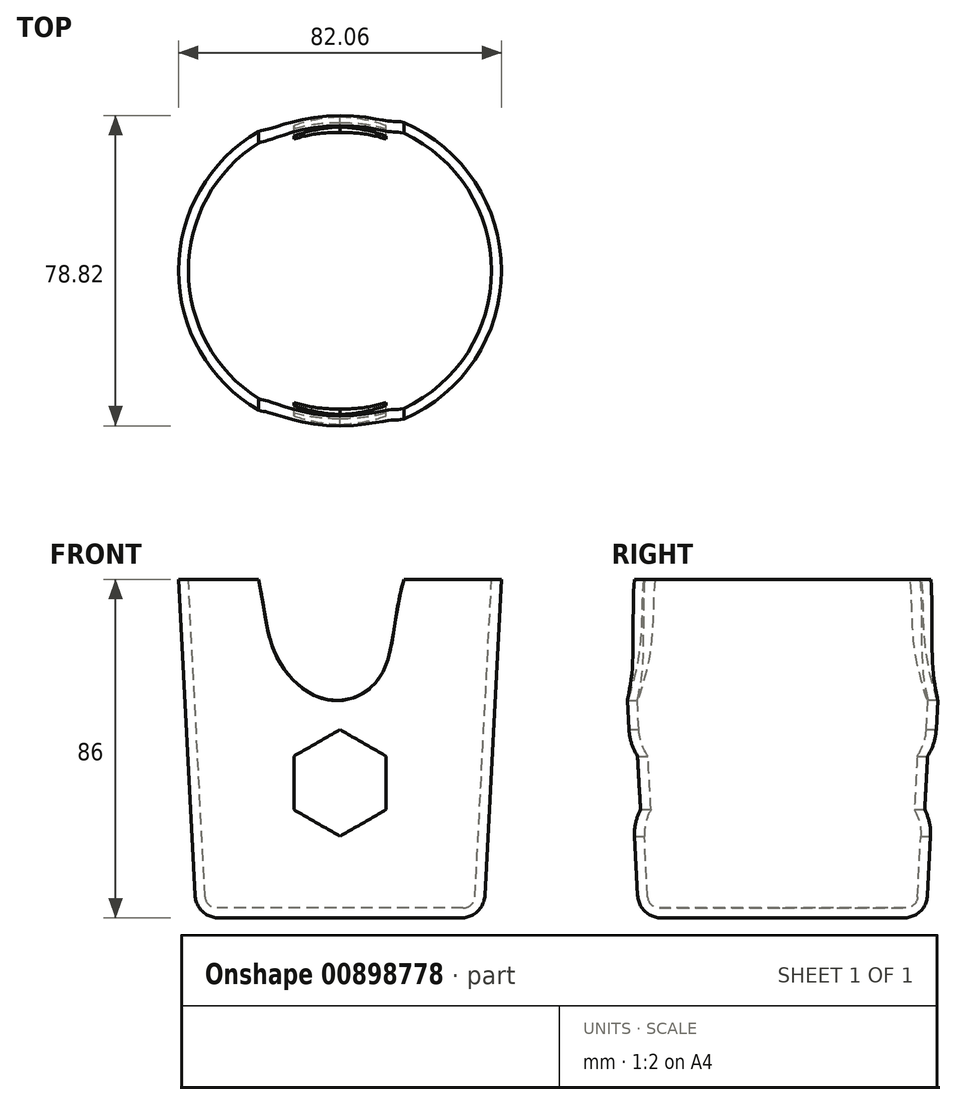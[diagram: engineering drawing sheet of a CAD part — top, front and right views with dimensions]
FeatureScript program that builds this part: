
annotation { "Feature Type Name" : "Feature", "Feature Type Description" : "" }
export const myFeature = defineFeature(function(context is Context, id is Id, definition is map)
    precondition{}
    {
        {
            var Q0;
            Q0=qCreatedBy(makeId("Top.planeOp"),FACE);
            var sketch = newSketch(context, id + "F0", { "sketchPlane" : qUnion([Q0])});
            skCircle(sketch, "E0", {"center": v(0, 0) * mm, "radius": 36.52 * mm});
            skSolve(sketch);
        }
        {
            var Q0;
            Q0=makeQuery(id+"F0.imprint","IMPRINT",FACE,{"disambiguationData":[TD([[makeQuery(id+"F0.imprint","IMPRINT",EDGE,{"derivedFrom":sQuery(id+"F0.wireOp",EDGE,"E0")}),1.0]])]});
            extrude(context, id + "F1", {"entities" : qUnion([Q0]), "depth" : 86 * mm, "offsetDistance" : 25 * mm, "hasDraft" : true, "draftAngle" : 3 * degree});
        }
        {
            var Q0;
            Q0=makeQuery(id+"F1.opExtrude","CAP_FACE",FACE,{"disambiguationData":[OSD([sQuery(id+"F0.wireOp",EDGE,"E0")])],"isStart":false});
            shell(context, id + "F2", {"entities" : qUnion([Q0]), "thickness" : 2.5 * mm});
        }
        {
            var Q0;
            Q0=qCreatedBy(makeId("Front.planeOp"),FACE);
            var sketch = newSketch(context, id + "F3", { "sketchPlane" : qUnion([Q0])});
            skCircle(sketch, "E1.cCircle", {"center": v(0, 34.28) * mm, "radius": 11.73 * mm, "construction": true});
            skLineSegment(sketch, "E1.0", {"start": v(11.73, 41.06) * mm, "end": v(11.73, 27.5) * mm});
            skLineSegment(sketch, "E1.1", {"start": v(11.73, 27.5) * mm, "end": v(0, 20.74) * mm});
            skLineSegment(sketch, "E1.2", {"start": v(0, 20.74) * mm, "end": v(-11.73, 27.5) * mm});
            skLineSegment(sketch, "E1.3", {"start": v(-11.73, 27.5) * mm, "end": v(-11.73, 41.06) * mm});
            skLineSegment(sketch, "E1.4", {"start": v(-11.73, 41.06) * mm, "end": v(0, 47.83) * mm});
            skLineSegment(sketch, "E1.5", {"start": v(0, 47.83) * mm, "end": v(11.73, 41.06) * mm});
            skPoint(sketch, "E1.0.midPoint", {"position": v(11.73, 34.28) * mm});
            skSolve(sketch);
        }
        {
            var Q0;
            Q0=makeQuery(id+"F3.imprint","IMPRINT",FACE,{"disambiguationData":[TD([[makeQuery(id+"F3.imprint","IMPRINT",EDGE,{"derivedFrom":sQuery(id+"F3.wireOp",EDGE,"E1.0")}),-1.0]])]});
            extrude(context, id + "F4", {"entities" : qUnion([Q0]), "operationType" : NewBodyOperationType.REMOVE, "endBound" : BoundingType.SYMMETRIC, "depth" : 135.2 * mm, "offsetDistance" : 25 * mm});
        }
        {
            var Q0;
            Q0=qCreatedBy(makeId("Front.planeOp"),FACE);
            var sketch = newSketch(context, id + "F5", { "sketchPlane" : qUnion([Q0])});
            skFitSpline(sketch, "E2", {"points": [v(-35.22, 110.41) * mm, v(-21.64, 89.24) * mm, v(-16.59, 67.45) * mm, v(-3.32, 55.44) * mm, v(9.95, 60.81) * mm, v(15.64, 83.87) * mm, v(29.28, 110.41) * mm], "startDerivative": vector(91.97, -112.85) * mm, "endDerivative": vector(88.8, 119.31) * mm});
            skLineSegment(sketch, "E3", {"start": v(-35.22, 110.41) * mm, "end": v(29.28, 110.41) * mm});
            skSolve(sketch);
        }
        {
            var Q0;
            Q0=makeQuery(id+"F5.imprint","IMPRINT",FACE,{"disambiguationData":[TD([[makeQuery(id+"F5.imprint","IMPRINT",EDGE,{"derivedFrom":sQuery(id+"F5.wireOp",EDGE,"E2")}),1.0]])]});
            extrude(context, id + "F6", {"entities" : qUnion([Q0]), "operationType" : NewBodyOperationType.REMOVE, "endBound" : BoundingType.SYMMETRIC, "depth" : 202 * mm, "offsetDistance" : 25 * mm});
        }
        {
            var Q0;
            {var subQ0=sQuery(id+"F0.wireOp",EDGE,"E0");Q0=makeQuery(id+"F2.opShell","OFFSET_EDGE",EDGE,{"disambiguationData":[OSD([subQ0]),TDD([makeQuery(id+"F1.opExtrude","CAP_EDGE",EDGE,{"disambiguationData":[OSD([subQ0])],"isStart":true})])]});}
            fillet(context, id + "F7", {"entities" : qUnion([Q0]), "radius" : 3 * mm, "tangentPropagation" : true, "allowEdgeOverflow" : false});
        }
        {
            var Q0;
            Q0=makeQuery(id+"F1.opExtrude","CAP_EDGE",EDGE,{"disambiguationData":[OSD([sQuery(id+"F0.wireOp",EDGE,"E0")])],"isStart":true});
            fillet(context, id + "F8", {"entities" : qUnion([Q0]), "radius" : 6 * mm, "tangentPropagation" : true, "allowEdgeOverflow" : false});
        }
    });
